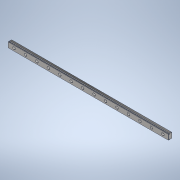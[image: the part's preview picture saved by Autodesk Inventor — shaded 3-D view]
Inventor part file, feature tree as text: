
AUTODESK INVENTOR PART (.ipt)
format: ipt  version: 2022 (Build 260153000, 153)  size: 179,200 bytes
history: imported  units: in
note: dims shown in document units (in); Inventor stores cm internally (conversion verified against a paired STEP export)
features: imported_body x1
ambient origin geometry x8: Origin, YZ Plane, XZ Plane, XY Plane, X Axis, Y Axis, Z Axis, Center Point
bodies: Solid1 (imported_parasolid), Body1 (imported_parasolid)
feature tree (1):
  imported_body  NMx_Import_Brep_tag  [imported B-rep: ~12 faces, bbox_mm=[349.5, 11.5, 4.5]]
